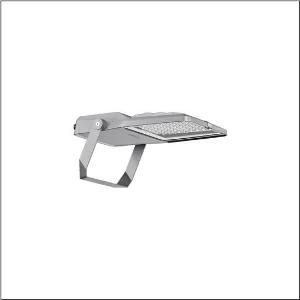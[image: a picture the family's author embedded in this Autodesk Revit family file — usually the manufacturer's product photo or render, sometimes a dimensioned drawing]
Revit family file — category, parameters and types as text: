
# Revit family: floodlight_fl_21_iq_mini___pl61_5xa7771d4c1a_f1b8
name_source: partatom
category: Lighting Fixtures
units: mm (PartAtom-declared; Revit-internal decimal feet)

## family parameters
Cut with Voids When Loaded = No
Host = Face
Light Source = No
Part Type = Normal
Room Calculation Point = No
Round Connector Dimension = Use Diameter
Shared = No

## types (1)
- --- (1 x LED, 18260 lm, 143 W, 4000K)
    Apparent Load = 143 VA
    CIE Flux Codes = 33 65 98 100 100
    Color Rendering = 70
    Color Temperature = 4000K
    Default Elevation = 1800 mm
    Description = Floodlight FL 21 iQ mini, floodlight, primary light control with lens, of PMMA, primary optical cover: protective disc, of toughened safety glass, transparent, light distribution: PL61, light emission: direct distribution, installation type: surface-mounted, LED, High Power LED, rated luminous flux: 18.260lm, luminous efficacy: 128lm/W, light colour: 740, colour temperature: 4000K, control: Auto-Match, Temp-Guard, Lumen-Switch, Night-Set, Smart-Wire, Light-Fading, Desk-Remote (wireless, voltage-free reading and setting of iQ features in the workshop via application-optimized NFC function/RFID function), optimised constant luminous flux control (CLO 2.0), with terminal, 6-pole, mains connection: 220..240V, AC, 50/60Hz, start of lifetime: 143W, end of service life: 152W, reduction: 61W, luminaire housing, of diecast aluminium, powder-coated, Siteco® metallic grey (DB 702S), corrosivity category C5 mid according to DIN EN ISO 12944, sealing non-destructively replaceable, mounting bracket, of steel, galvanised, powder-coated, Siteco® metallic grey (DB 702S), protection rating (complete): IP66, insulation class (complete): insulation class II (safety insulation), certification: CE, ENEC, VDE, protection symbol: D, impact resistance: IK08, permissible operating ambient temperature: -40..+40°C, permissible operating ambient temperature for outdoor applications: -40..+50°C, standard: DIN EN 12944, LABS conformity tested according to VDMA 24364:2018-05, packaging unit: 1 piece

Light Distribution: PL61
    Height = 70 mm
    Lamp = 1 x LED
    Lamp Light Flux = 18260 lm
    Lamp Power = 143 W
    Lamp count = 1
    Length = 485 mm
    Luminous efficacy = 128 lm/W
    Manufacturer = Siteco
    ModVariant = No
    Model = 5XA7771D4C1A
    Number of Poles = 1
    OnlyDefault = Yes
    Power Factor = 1
    Product Name = Floodlight FL 21 iQ mini | PL61
    Product group = floodlight | pylon annexe
    ProductGroupID = 6200
    Protection Class = Protection class II
    Protection Degree = IP 66
    RLX_Detail_Level = 1
    RLX_Emergency_Light_Flux = 0 lm
    RLX_Emergency_Type = 0
    RLX_Emergency_Type_DB = No
    RlxData = <blob elided: 96413 chars, md5=226e2e2c>
    Socket = socket
    Standby Power = 0 W
    System Light Flux = 18260 lm
    System Power = 143 W
    Type Comments = factory setting: luminous flux: 100 % | dim-lin: 254 | 730 mA
    Type Image = l_1006845.jpg
    URL = http://relux.com
    VarID = @adj_105755
    Voltage = 0 V
    Weight = 0.00 kg
    Width = 337 mm

## geometry (parser evidence)
native form markers: Blend x4, Sweep x15
no freeform markers — native parametric forms only
